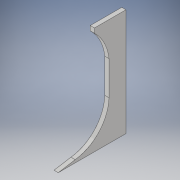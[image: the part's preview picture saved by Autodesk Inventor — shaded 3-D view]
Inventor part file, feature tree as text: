
AUTODESK INVENTOR PART (.ipt)
format: ipt  version: 2018 (Build 220112000, 112)  size: 132,608 bytes
history: native  units: in
note: dims shown in document units (in); Inventor stores cm internally (conversion verified against a paired STEP export)
features: extrude x1, sketch x1
ambient origin geometry x8: Origin, YZ Plane, XZ Plane, XY Plane, X Axis, Y Axis, Z Axis, Center Point
bodies: Solid1 (feature_tree)
feature tree (2):
  extrude  "Extrusion1"  Depth=12.0in
  sketch  "Sketch1"  dims[d0=13.0in d1=12.0in d2=19.0in d3=3.0in d4=6.0in d5=8.25in d9=9.0in d13=8.625in d16=0.268in d17=0.134in d19=3.0in d20=3.0in d25=0.5in d39=7.5in d40=6.0in d41=0.5in d42=6.375in d43=135.0deg d44=7.0in d45=0.75in d46=0.0in]
